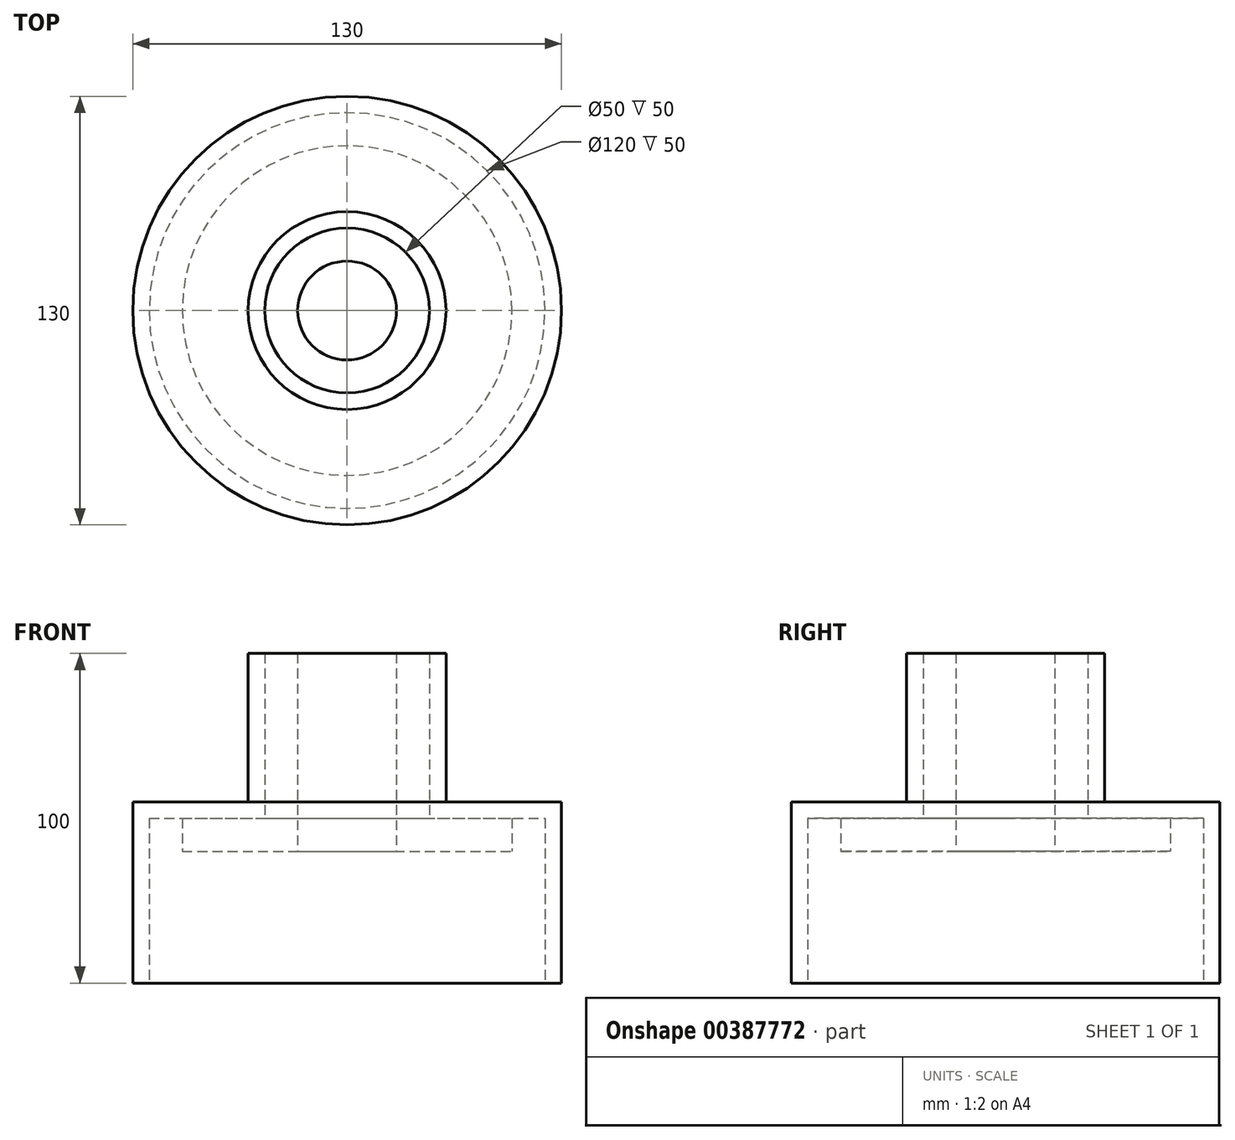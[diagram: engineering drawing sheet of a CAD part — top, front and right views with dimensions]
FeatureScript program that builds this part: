
annotation { "Feature Type Name" : "Feature", "Feature Type Description" : "" }
export const myFeature = defineFeature(function(context is Context, id is Id, definition is map)
    precondition{}
    {
        {
            var Q0;
            Q0=qCreatedBy(makeId("Front.planeOp"),FACE);
            var sketch = newSketch(context, id + "F0", { "sketchPlane" : qUnion([Q0])});
            skLineSegment(sketch, "E0", {"start": v(-30, 50) * mm, "end": v(-30, 5) * mm});
            skLineSegment(sketch, "E1", {"start": v(-30, 5) * mm, "end": v(-65, 5) * mm});
            skLineSegment(sketch, "E2", {"start": v(-65, 5) * mm, "end": v(-65, -50) * mm});
            skLineSegment(sketch, "E3", {"start": v(-65, -50) * mm, "end": v(-60, -50) * mm});
            skLineSegment(sketch, "E4", {"start": v(-60, -50) * mm, "end": v(-60, 0) * mm});
            skLineSegment(sketch, "E5", {"start": v(-60, 0) * mm, "end": v(-25, 0) * mm});
            skLineSegment(sketch, "E6", {"start": v(-25, 0) * mm, "end": v(-25, 50) * mm});
            skLineSegment(sketch, "E7", {"start": v(-30, 50) * mm, "end": v(-25, 50) * mm});
            skLineSegment(sketch, "E8", {"start": v(-50, 0) * mm, "end": v(-50, -10) * mm});
            skLineSegment(sketch, "E9", {"start": v(-50, -10) * mm, "end": v(-15, -10) * mm});
            skLineSegment(sketch, "E10", {"start": v(-15, -10) * mm, "end": v(-15, 50) * mm});
            skLineSegment(sketch, "E11", {"start": v(-15, 50) * mm, "end": v(-25, 50) * mm});
            skLineSegment(sketch, "E12", {"start": v(0, 0) * mm, "end": v(0, 84.17) * mm, "construction": true});
            skSolve(sketch);
        }
        {
            var Q0;
            Q0=makeQuery(id+"F0.imprint","IMPRINT",FACE,{"disambiguationData":[TD([[makeQuery(id+"F0.imprint","IMPRINT",EDGE,{"derivedFrom":sQuery(id+"F0.wireOp",EDGE,"E0")}),1.0]])]});
            var Q1;
            Q1=sQuery(id+"F0.wireOp",EDGE,"E12");
            revolve(context, id + "F1", {"entities" : qUnion([Q0]), "axis" : qUnion([Q1]), "revolveType" : RevolveType.FULL});
        }
        {
            var Q0;
            {var subQ1=sQuery(id+"F0.wireOp",EDGE,"E6");Q0=makeQuery(id+"F0.imprint","IMPRINT",FACE,{"disambiguationData":[TD([[makeQuery(id+"F0.imprint","IMPRINT",EDGE,{"derivedFrom":subQ1}),-1.0]])]});}
            var Q1;
            Q1=sQuery(id+"F0.wireOp",EDGE,"E12");
            revolve(context, id + "F2", {"entities" : qUnion([Q0]), "axis" : qUnion([Q1]), "revolveType" : RevolveType.FULL});
        }
    });
